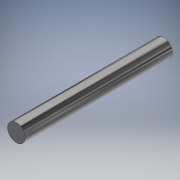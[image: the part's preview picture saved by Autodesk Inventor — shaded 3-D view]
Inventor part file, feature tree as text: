
AUTODESK INVENTOR PART (.ipt)
format: ipt  version: 2019.4 (Build 234330000, 330)  size: 99,328 bytes
history: native  units: mm
features: extrude x1, sketch x1
ambient origin geometry x8: Origin, YZ Plane, XZ Plane, XY Plane, X Axis, Y Axis, Z Axis, Center Point
bodies: Solid1 (feature_tree)
feature tree (2):
  extrude  "Extrusion1"  Depth=25.0mm TaperAngle=0.0deg
  sketch  "Sketch1"  dims[d0=3.0mm d1=25.0mm d2=0.0mm]
